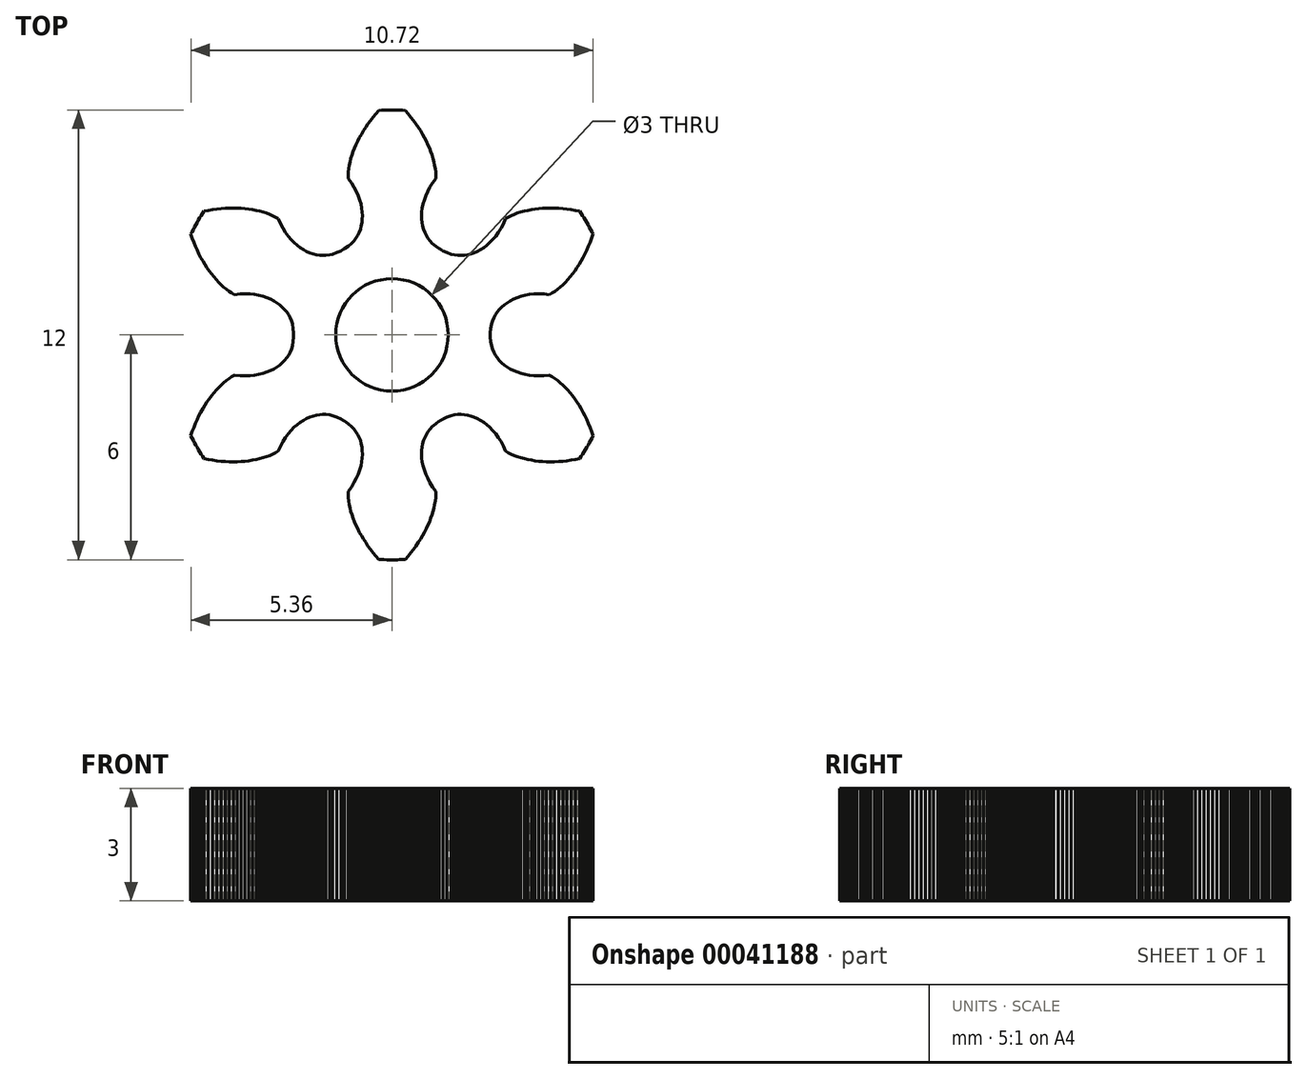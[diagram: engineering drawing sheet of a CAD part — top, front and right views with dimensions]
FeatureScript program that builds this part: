
annotation { "Feature Type Name" : "Feature", "Feature Type Description" : "" }
export const myFeature = defineFeature(function(context is Context, id is Id, definition is map)
    precondition{}
    {
        {
            var Q0;
            Q0=qCreatedBy(makeId("Top.planeOp"),FACE);
            var sketch = newSketch(context, id + "F0", { "sketchPlane" : qUnion([Q0])});
            skLineSegment(sketch, "E0", {"start": v(2.62, 0) * mm, "end": v(2.62, 0.01) * mm});
            skLineSegment(sketch, "E1", {"start": v(2.62, 0.01) * mm, "end": v(2.62, 0.02) * mm});
            skLineSegment(sketch, "E2", {"start": v(2.62, 0.02) * mm, "end": v(2.62, 0.03) * mm});
            skLineSegment(sketch, "E3", {"start": v(2.62, 0.03) * mm, "end": v(2.62, 0.05) * mm});
            skLineSegment(sketch, "E4", {"start": v(2.62, 0.05) * mm, "end": v(2.62, 0.06) * mm});
            skLineSegment(sketch, "E5", {"start": v(2.62, 0.06) * mm, "end": v(2.63, 0.17) * mm});
            skLineSegment(sketch, "E6", {"start": v(2.63, 0.17) * mm, "end": v(2.65, 0.3) * mm});
            skLineSegment(sketch, "E7", {"start": v(2.65, 0.3) * mm, "end": v(2.68, 0.38) * mm});
            skLineSegment(sketch, "E8", {"start": v(2.68, 0.38) * mm, "end": v(2.72, 0.46) * mm});
            skLineSegment(sketch, "E9", {"start": v(2.72, 0.46) * mm, "end": v(2.76, 0.54) * mm});
            skLineSegment(sketch, "E10", {"start": v(2.76, 0.54) * mm, "end": v(2.8, 0.6) * mm});
            skLineSegment(sketch, "E11", {"start": v(2.8, 0.6) * mm, "end": v(2.86, 0.68) * mm});
            skLineSegment(sketch, "E12", {"start": v(2.86, 0.68) * mm, "end": v(2.93, 0.74) * mm});
            skLineSegment(sketch, "E13", {"start": v(2.93, 0.74) * mm, "end": v(3, 0.8) * mm});
            skLineSegment(sketch, "E14", {"start": v(3, 0.8) * mm, "end": v(3.07, 0.86) * mm});
            skLineSegment(sketch, "E15", {"start": v(3.07, 0.86) * mm, "end": v(3.15, 0.9) * mm});
            skLineSegment(sketch, "E16", {"start": v(3.15, 0.9) * mm, "end": v(3.24, 0.95) * mm});
            skLineSegment(sketch, "E17", {"start": v(3.24, 0.95) * mm, "end": v(3.34, 1) * mm});
            skLineSegment(sketch, "E18", {"start": v(3.34, 1) * mm, "end": v(3.44, 1.03) * mm});
            skLineSegment(sketch, "E19", {"start": v(3.44, 1.03) * mm, "end": v(3.55, 1.05) * mm});
            skLineSegment(sketch, "E20", {"start": v(3.55, 1.05) * mm, "end": v(3.66, 1.08) * mm});
            skLineSegment(sketch, "E21", {"start": v(3.66, 1.08) * mm, "end": v(3.79, 1.09) * mm});
            skLineSegment(sketch, "E22", {"start": v(3.79, 1.09) * mm, "end": v(3.92, 1.1) * mm});
            skLineSegment(sketch, "E23", {"start": v(3.92, 1.1) * mm, "end": v(4.05, 1.1) * mm});
            skLineSegment(sketch, "E24", {"start": v(4.05, 1.1) * mm, "end": v(4.2, 1.07) * mm});
            skLineSegment(sketch, "E25", {"start": v(4.2, 1.07) * mm, "end": v(4.27, 1.12) * mm});
            skLineSegment(sketch, "E26", {"start": v(4.27, 1.12) * mm, "end": v(4.35, 1.16) * mm});
            skLineSegment(sketch, "E27", {"start": v(4.35, 1.16) * mm, "end": v(4.42, 1.22) * mm});
            skLineSegment(sketch, "E28", {"start": v(4.42, 1.22) * mm, "end": v(4.49, 1.28) * mm});
            skLineSegment(sketch, "E29", {"start": v(4.49, 1.28) * mm, "end": v(4.56, 1.34) * mm});
            skLineSegment(sketch, "E30", {"start": v(4.56, 1.34) * mm, "end": v(4.62, 1.4) * mm});
            skLineSegment(sketch, "E31", {"start": v(4.62, 1.4) * mm, "end": v(4.69, 1.47) * mm});
            skLineSegment(sketch, "E32", {"start": v(4.69, 1.47) * mm, "end": v(4.75, 1.55) * mm});
            skLineSegment(sketch, "E33", {"start": v(4.75, 1.55) * mm, "end": v(4.82, 1.63) * mm});
            skLineSegment(sketch, "E34", {"start": v(4.82, 1.63) * mm, "end": v(4.88, 1.7) * mm});
            skLineSegment(sketch, "E35", {"start": v(4.88, 1.7) * mm, "end": v(4.93, 1.8) * mm});
            skLineSegment(sketch, "E36", {"start": v(4.93, 1.8) * mm, "end": v(5, 1.88) * mm});
            skLineSegment(sketch, "E37", {"start": v(5, 1.88) * mm, "end": v(5.05, 1.97) * mm});
            skLineSegment(sketch, "E38", {"start": v(5.05, 1.97) * mm, "end": v(5.1, 2.06) * mm});
            skLineSegment(sketch, "E39", {"start": v(5.1, 2.06) * mm, "end": v(5.15, 2.16) * mm});
            skLineSegment(sketch, "E40", {"start": v(5.15, 2.16) * mm, "end": v(5.2, 2.26) * mm});
            skLineSegment(sketch, "E41", {"start": v(5.2, 2.26) * mm, "end": v(5.24, 2.36) * mm});
            skLineSegment(sketch, "E42", {"start": v(5.24, 2.36) * mm, "end": v(5.28, 2.47) * mm});
            skLineSegment(sketch, "E43", {"start": v(5.28, 2.47) * mm, "end": v(5.33, 2.58) * mm});
            skLineSegment(sketch, "E44", {"start": v(5.33, 2.58) * mm, "end": v(5.36, 2.69) * mm});
            skLineSegment(sketch, "E45", {"start": v(5.36, 2.69) * mm, "end": v(5.33, 2.75) * mm});
            skLineSegment(sketch, "E46", {"start": v(5.33, 2.75) * mm, "end": v(5.3, 2.81) * mm});
            skLineSegment(sketch, "E47", {"start": v(5.3, 2.81) * mm, "end": v(5.27, 2.88) * mm});
            skLineSegment(sketch, "E48", {"start": v(5.27, 2.88) * mm, "end": v(5.23, 2.94) * mm});
            skLineSegment(sketch, "E49", {"start": v(5.23, 2.94) * mm, "end": v(5.2, 3) * mm});
            skPoint(sketch, "E50", {"position": v(0, 0) * mm});
            skLineSegment(sketch, "E51", {"start": v(0, 0) * mm, "end": v(4.5, 0) * mm, "construction": true});
            skLineSegment(sketch, "E52", {"start": v(4.5, 0) * mm, "end": v(5.4, 0) * mm, "construction": true});
            skLineSegment(sketch, "E53.MirrorCS", {"start": v(2.62, 0) * mm, "end": v(2.62, -0.01) * mm});
            skLineSegment(sketch, "E54.MirrorCS", {"start": v(2.62, -0.01) * mm, "end": v(2.62, -0.02) * mm});
            skLineSegment(sketch, "E55.MirrorCS", {"start": v(2.62, -0.02) * mm, "end": v(2.62, -0.03) * mm});
            skLineSegment(sketch, "E56.MirrorCS", {"start": v(2.62, -0.05) * mm, "end": v(2.62, -0.06) * mm});
            skLineSegment(sketch, "E57.MirrorCS", {"start": v(2.62, -0.03) * mm, "end": v(2.62, -0.05) * mm});
            skLineSegment(sketch, "E58.MirrorCS", {"start": v(2.62, -0.06) * mm, "end": v(2.63, -0.17) * mm});
            skLineSegment(sketch, "E59.MirrorCS", {"start": v(3.55, -1.05) * mm, "end": v(3.66, -1.08) * mm});
            skLineSegment(sketch, "E60.MirrorCS", {"start": v(3.92, -1.1) * mm, "end": v(4.05, -1.1) * mm});
            skLineSegment(sketch, "E61.MirrorCS", {"start": v(3.66, -1.08) * mm, "end": v(3.79, -1.09) * mm});
            skLineSegment(sketch, "E62.MirrorCS", {"start": v(3.79, -1.09) * mm, "end": v(3.92, -1.1) * mm});
            skLineSegment(sketch, "E63.MirrorCS", {"start": v(5.33, -2.75) * mm, "end": v(5.3, -2.81) * mm});
            skLineSegment(sketch, "E64.MirrorCS", {"start": v(4.49, -1.28) * mm, "end": v(4.56, -1.34) * mm});
            skLineSegment(sketch, "E65.MirrorCS", {"start": v(4.27, -1.12) * mm, "end": v(4.35, -1.16) * mm});
            skLineSegment(sketch, "E66.MirrorCS", {"start": v(4.82, -1.63) * mm, "end": v(4.88, -1.7) * mm});
            skLineSegment(sketch, "E67.MirrorCS", {"start": v(4.35, -1.16) * mm, "end": v(4.42, -1.22) * mm});
            skLineSegment(sketch, "E68.MirrorCS", {"start": v(4.93, -1.8) * mm, "end": v(5, -1.88) * mm});
            skLineSegment(sketch, "E69.MirrorCS", {"start": v(5.1, -2.06) * mm, "end": v(5.15, -2.16) * mm});
            skLineSegment(sketch, "E70.MirrorCS", {"start": v(2.86, -0.68) * mm, "end": v(2.93, -0.74) * mm});
            skLineSegment(sketch, "E71.MirrorCS", {"start": v(3.44, -1.03) * mm, "end": v(3.55, -1.05) * mm});
            skLineSegment(sketch, "E72.MirrorCS", {"start": v(2.8, -0.6) * mm, "end": v(2.86, -0.68) * mm});
            skLineSegment(sketch, "E73.MirrorCS", {"start": v(5, -1.88) * mm, "end": v(5.05, -1.97) * mm});
            skLineSegment(sketch, "E74.MirrorCS", {"start": v(2.72, -0.46) * mm, "end": v(2.76, -0.54) * mm});
            skLineSegment(sketch, "E75.MirrorCS", {"start": v(3.24, -0.95) * mm, "end": v(3.34, -1) * mm});
            skLineSegment(sketch, "E76.MirrorCS", {"start": v(2.68, -0.38) * mm, "end": v(2.72, -0.46) * mm});
            skLineSegment(sketch, "E77.MirrorCS", {"start": v(2.65, -0.3) * mm, "end": v(2.68, -0.38) * mm});
            skLineSegment(sketch, "E78.MirrorCS", {"start": v(2.63, -0.17) * mm, "end": v(2.65, -0.3) * mm});
            skLineSegment(sketch, "E79.MirrorCS", {"start": v(2.76, -0.54) * mm, "end": v(2.8, -0.6) * mm});
            skLineSegment(sketch, "E80.MirrorCS", {"start": v(5.24, -2.36) * mm, "end": v(5.28, -2.47) * mm});
            skLineSegment(sketch, "E81.MirrorCS", {"start": v(2.93, -0.74) * mm, "end": v(3, -0.8) * mm});
            skLineSegment(sketch, "E82.MirrorCS", {"start": v(4.88, -1.7) * mm, "end": v(4.93, -1.8) * mm});
            skLineSegment(sketch, "E83.MirrorCS", {"start": v(4.69, -1.47) * mm, "end": v(4.75, -1.55) * mm});
            skLineSegment(sketch, "E84.MirrorCS", {"start": v(5.27, -2.88) * mm, "end": v(5.23, -2.94) * mm});
            skLineSegment(sketch, "E85.MirrorCS", {"start": v(4.75, -1.55) * mm, "end": v(4.82, -1.63) * mm});
            skLineSegment(sketch, "E86.MirrorCS", {"start": v(3, -0.8) * mm, "end": v(3.07, -0.86) * mm});
            skLineSegment(sketch, "E87.MirrorCS", {"start": v(5.23, -2.94) * mm, "end": v(5.2, -3) * mm});
            skLineSegment(sketch, "E88.MirrorCS", {"start": v(3.07, -0.86) * mm, "end": v(3.15, -0.9) * mm});
            skLineSegment(sketch, "E89.MirrorCS", {"start": v(5.05, -1.97) * mm, "end": v(5.1, -2.06) * mm});
            skLineSegment(sketch, "E90.MirrorCS", {"start": v(5.15, -2.16) * mm, "end": v(5.2, -2.26) * mm});
            skLineSegment(sketch, "E91.MirrorCS", {"start": v(4.42, -1.22) * mm, "end": v(4.49, -1.28) * mm});
            skLineSegment(sketch, "E92.MirrorCS", {"start": v(4.05, -1.1) * mm, "end": v(4.2, -1.07) * mm});
            skLineSegment(sketch, "E93.MirrorCS", {"start": v(5.33, -2.58) * mm, "end": v(5.36, -2.69) * mm});
            skLineSegment(sketch, "E94.MirrorCS", {"start": v(4.56, -1.34) * mm, "end": v(4.62, -1.4) * mm});
            skLineSegment(sketch, "E95.MirrorCS", {"start": v(4.2, -1.07) * mm, "end": v(4.27, -1.12) * mm});
            skLineSegment(sketch, "E96.MirrorCS", {"start": v(5.2, -2.26) * mm, "end": v(5.24, -2.36) * mm});
            skLineSegment(sketch, "E97.MirrorCS", {"start": v(3.34, -1) * mm, "end": v(3.44, -1.03) * mm});
            skLineSegment(sketch, "E98.MirrorCS", {"start": v(4.62, -1.4) * mm, "end": v(4.69, -1.47) * mm});
            skLineSegment(sketch, "E99.MirrorCS", {"start": v(5.28, -2.47) * mm, "end": v(5.33, -2.58) * mm});
            skLineSegment(sketch, "E100.MirrorCS", {"start": v(5.3, -2.81) * mm, "end": v(5.27, -2.88) * mm});
            skLineSegment(sketch, "E101.MirrorCS", {"start": v(3.15, -0.9) * mm, "end": v(3.24, -0.95) * mm});
            skLineSegment(sketch, "E102.MirrorCS", {"start": v(5.36, -2.69) * mm, "end": v(5.33, -2.75) * mm});
            skLineSegment(sketch, "E103.1.0", {"start": v(3.03, 3.1) * mm, "end": v(3.1, 3.14) * mm});
            skLineSegment(sketch, "E103.1.1", {"start": v(1.12, 4.61) * mm, "end": v(1.1, 4.7) * mm});
            skLineSegment(sketch, "E103.1.2", {"start": v(4.9, 3.32) * mm, "end": v(5.01, 3.3) * mm});
            skLineSegment(sketch, "E103.1.3", {"start": v(1.85, 2.12) * mm, "end": v(1.93, 2.13) * mm});
            skLineSegment(sketch, "E103.1.4", {"start": v(5.05, 3.24) * mm, "end": v(5.09, 3.18) * mm});
            skLineSegment(sketch, "E103.1.5", {"start": v(1.15, 4.43) * mm, "end": v(1.14, 4.52) * mm});
            skLineSegment(sketch, "E103.1.6", {"start": v(0.28, 6) * mm, "end": v(0.21, 6) * mm});
            skLineSegment(sketch, "E103.1.7", {"start": v(0.7, 5.54) * mm, "end": v(0.64, 5.63) * mm});
            skLineSegment(sketch, "E103.1.8", {"start": v(1.08, 4.06) * mm, "end": v(1.17, 4.17) * mm});
            skLineSegment(sketch, "E103.1.9", {"start": v(4.23, 3.38) * mm, "end": v(4.34, 3.38) * mm});
            skLineSegment(sketch, "E103.1.10", {"start": v(1.58, 2.15) * mm, "end": v(1.67, 2.13) * mm});
            skLineSegment(sketch, "E103.1.11", {"start": v(0.43, 5.9) * mm, "end": v(0.35, 5.99) * mm});
            skLineSegment(sketch, "E103.1.12", {"start": v(0.64, 5.63) * mm, "end": v(0.57, 5.72) * mm});
            skLineSegment(sketch, "E103.1.13", {"start": v(4.67, 3.36) * mm, "end": v(4.78, 3.34) * mm});
            skLineSegment(sketch, "E103.1.14", {"start": v(0.57, 5.72) * mm, "end": v(0.5, 5.81) * mm});
            skLineSegment(sketch, "E103.1.15", {"start": v(1.17, 4.26) * mm, "end": v(1.16, 4.35) * mm});
            skLineSegment(sketch, "E103.1.16", {"start": v(3.26, 3.22) * mm, "end": v(3.35, 3.25) * mm});
            skLineSegment(sketch, "E103.1.17", {"start": v(2.45, 2.33) * mm, "end": v(2.53, 2.4) * mm});
            skLineSegment(sketch, "E103.1.18", {"start": v(2.9, 2.85) * mm, "end": v(2.97, 2.96) * mm});
            skLineSegment(sketch, "E103.1.19", {"start": v(0.5, 5.81) * mm, "end": v(0.43, 5.9) * mm});
            skLineSegment(sketch, "E103.1.20", {"start": v(1.16, 4.35) * mm, "end": v(1.15, 4.43) * mm});
            skLineSegment(sketch, "E103.1.21", {"start": v(1.67, 2.13) * mm, "end": v(1.76, 2.12) * mm});
            skLineSegment(sketch, "E103.1.22", {"start": v(2.97, 2.96) * mm, "end": v(3.03, 3.1) * mm});
            skLineSegment(sketch, "E103.1.23", {"start": v(2.84, 2.74) * mm, "end": v(2.9, 2.85) * mm});
            skLineSegment(sketch, "E103.1.24", {"start": v(0.35, 5.99) * mm, "end": v(0.28, 6) * mm});
            skLineSegment(sketch, "E103.1.25", {"start": v(1.14, 4.52) * mm, "end": v(1.12, 4.61) * mm});
            skLineSegment(sketch, "E103.1.26", {"start": v(3.44, 3.28) * mm, "end": v(3.53, 3.3) * mm});
            skLineSegment(sketch, "E103.1.27", {"start": v(3.35, 3.25) * mm, "end": v(3.44, 3.28) * mm});
            skLineSegment(sketch, "E103.1.28", {"start": v(0.21, 6) * mm, "end": v(0.14, 6) * mm});
            skLineSegment(sketch, "E103.1.29", {"start": v(4.56, 3.37) * mm, "end": v(4.67, 3.36) * mm});
            skLineSegment(sketch, "E103.1.30", {"start": v(1.1, 4.7) * mm, "end": v(1.07, 4.8) * mm});
            skLineSegment(sketch, "E103.1.31", {"start": v(0.82, 2.9) * mm, "end": v(0.8, 3) * mm});
            skLineSegment(sketch, "E103.1.32", {"start": v(0.8, 3) * mm, "end": v(0.8, 3.09) * mm});
            skLineSegment(sketch, "E103.1.33", {"start": v(0.8, 3.09) * mm, "end": v(0.8, 3.18) * mm});
            skLineSegment(sketch, "E103.1.34", {"start": v(0.95, 3.82) * mm, "end": v(1.01, 3.94) * mm});
            skLineSegment(sketch, "E103.1.35", {"start": v(2.61, 2.46) * mm, "end": v(2.69, 2.55) * mm});
            skLineSegment(sketch, "E103.1.36", {"start": v(0.82, 5.35) * mm, "end": v(0.76, 5.45) * mm});
            skLineSegment(sketch, "E103.1.37", {"start": v(1.17, 2.37) * mm, "end": v(1.07, 2.44) * mm});
            skLineSegment(sketch, "E103.1.38", {"start": v(1.07, 2.44) * mm, "end": v(1.01, 2.5) * mm});
            skLineSegment(sketch, "E103.1.39", {"start": v(1.01, 2.5) * mm, "end": v(0.96, 2.58) * mm});
            skLineSegment(sketch, "E103.1.40", {"start": v(5.16, 3.06) * mm, "end": v(5.2, 3) * mm});
            skLineSegment(sketch, "E103.1.41", {"start": v(0.96, 2.58) * mm, "end": v(0.91, 2.66) * mm});
            skLineSegment(sketch, "E103.1.42", {"start": v(0.91, 2.66) * mm, "end": v(0.88, 2.74) * mm});
            skLineSegment(sketch, "E103.1.43", {"start": v(0.88, 2.74) * mm, "end": v(0.84, 2.82) * mm});
            skLineSegment(sketch, "E103.1.44", {"start": v(0.84, 2.82) * mm, "end": v(0.82, 2.9) * mm});
            skLineSegment(sketch, "E103.1.45", {"start": v(2.53, 2.4) * mm, "end": v(2.61, 2.46) * mm});
            skLineSegment(sketch, "E103.1.46", {"start": v(0.8, 3.18) * mm, "end": v(0.8, 3.28) * mm});
            skLineSegment(sketch, "E103.1.47", {"start": v(2.1, 2.16) * mm, "end": v(2.2, 2.2) * mm});
            skLineSegment(sketch, "E103.1.48", {"start": v(0.14, 6) * mm, "end": v(0.07, 6) * mm});
            skLineSegment(sketch, "E103.1.49", {"start": v(3.1, 3.14) * mm, "end": v(3.18, 3.18) * mm});
            skLineSegment(sketch, "E103.1.50", {"start": v(1.07, 4.8) * mm, "end": v(1.04, 4.9) * mm});
            skLineSegment(sketch, "E103.1.51", {"start": v(1.01, 3.94) * mm, "end": v(1.08, 4.06) * mm});
            skLineSegment(sketch, "E103.1.52", {"start": v(0.76, 5.45) * mm, "end": v(0.7, 5.54) * mm});
            skLineSegment(sketch, "E103.1.53", {"start": v(2.28, 2.23) * mm, "end": v(2.36, 2.28) * mm});
            skLineSegment(sketch, "E103.1.54", {"start": v(1.93, 2.13) * mm, "end": v(2.02, 2.14) * mm});
            skLineSegment(sketch, "E103.1.55", {"start": v(0.8, 3.28) * mm, "end": v(0.8, 3.39) * mm});
            skLineSegment(sketch, "E103.1.56", {"start": v(3.92, 3.37) * mm, "end": v(4.02, 3.38) * mm});
            skLineSegment(sketch, "E103.1.57", {"start": v(3.82, 3.36) * mm, "end": v(3.92, 3.37) * mm});
            skLineSegment(sketch, "E103.1.58", {"start": v(0.07, 6) * mm, "end": v(0, 6) * mm});
            skLineSegment(sketch, "E103.1.59", {"start": v(1.04, 4.9) * mm, "end": v(1, 4.98) * mm});
            skLineSegment(sketch, "E103.1.60", {"start": v(3.53, 3.3) * mm, "end": v(3.62, 3.32) * mm});
            skLineSegment(sketch, "E103.1.61", {"start": v(3.18, 3.18) * mm, "end": v(3.26, 3.22) * mm});
            skLineSegment(sketch, "E103.1.62", {"start": v(4.12, 3.38) * mm, "end": v(4.23, 3.38) * mm});
            skLineSegment(sketch, "E103.1.63", {"start": v(3.62, 3.32) * mm, "end": v(3.72, 3.34) * mm});
            skLineSegment(sketch, "E103.1.64", {"start": v(0.8, 3.39) * mm, "end": v(0.83, 3.5) * mm});
            skLineSegment(sketch, "E103.1.65", {"start": v(1, 4.98) * mm, "end": v(0.96, 5.08) * mm});
            skLineSegment(sketch, "E103.1.66", {"start": v(4.78, 3.34) * mm, "end": v(4.9, 3.32) * mm});
            skLineSegment(sketch, "E103.1.67", {"start": v(0.83, 3.5) * mm, "end": v(0.86, 3.6) * mm});
            skLineSegment(sketch, "E103.1.68", {"start": v(5.12, 3.12) * mm, "end": v(5.16, 3.06) * mm});
            skLineSegment(sketch, "E103.1.69", {"start": v(4.02, 3.38) * mm, "end": v(4.12, 3.38) * mm});
            skLineSegment(sketch, "E103.1.70", {"start": v(0.96, 5.08) * mm, "end": v(0.92, 5.17) * mm});
            skLineSegment(sketch, "E103.1.71", {"start": v(5.09, 3.18) * mm, "end": v(5.12, 3.12) * mm});
            skLineSegment(sketch, "E103.1.72", {"start": v(0.86, 3.6) * mm, "end": v(0.9, 3.71) * mm});
            skLineSegment(sketch, "E103.1.73", {"start": v(4.34, 3.38) * mm, "end": v(4.45, 3.38) * mm});
            skLineSegment(sketch, "E103.1.74", {"start": v(3.72, 3.34) * mm, "end": v(3.82, 3.36) * mm});
            skLineSegment(sketch, "E103.1.75", {"start": v(0.92, 5.17) * mm, "end": v(0.87, 5.26) * mm});
            skLineSegment(sketch, "E103.1.76", {"start": v(2.36, 2.28) * mm, "end": v(2.45, 2.33) * mm});
            skLineSegment(sketch, "E103.1.77", {"start": v(4.45, 3.38) * mm, "end": v(4.56, 3.37) * mm});
            skLineSegment(sketch, "E103.1.78", {"start": v(1.17, 4.17) * mm, "end": v(1.17, 4.26) * mm});
            skLineSegment(sketch, "E103.1.79", {"start": v(1.76, 2.12) * mm, "end": v(1.85, 2.12) * mm});
            skLineSegment(sketch, "E103.1.80", {"start": v(0.9, 3.71) * mm, "end": v(0.95, 3.82) * mm});
            skLineSegment(sketch, "E103.1.81", {"start": v(2.2, 2.2) * mm, "end": v(2.28, 2.23) * mm});
            skLineSegment(sketch, "E103.1.82", {"start": v(2.02, 2.14) * mm, "end": v(2.1, 2.16) * mm});
            skLineSegment(sketch, "E103.1.83", {"start": v(0.87, 5.26) * mm, "end": v(0.82, 5.35) * mm});
            skLineSegment(sketch, "E103.1.84", {"start": v(5.01, 3.3) * mm, "end": v(5.05, 3.24) * mm});
            skLineSegment(sketch, "E103.1.85", {"start": v(2.76, 2.64) * mm, "end": v(2.84, 2.74) * mm});
            skLineSegment(sketch, "E103.1.86", {"start": v(2.69, 2.55) * mm, "end": v(2.76, 2.64) * mm});
            skLineSegment(sketch, "E103.1.87", {"start": v(1.47, 2.2) * mm, "end": v(1.58, 2.15) * mm});
            skLineSegment(sketch, "E103.1.88", {"start": v(1.36, 2.24) * mm, "end": v(1.47, 2.2) * mm});
            skLineSegment(sketch, "E103.1.89", {"start": v(1.34, 2.26) * mm, "end": v(1.35, 2.25) * mm});
            skLineSegment(sketch, "E103.1.90", {"start": v(1.31, 2.27) * mm, "end": v(1.3, 2.28) * mm});
            skLineSegment(sketch, "E103.1.91", {"start": v(1.27, 2.3) * mm, "end": v(1.26, 2.3) * mm});
            skLineSegment(sketch, "E103.1.92", {"start": v(1.26, 2.3) * mm, "end": v(1.17, 2.37) * mm});
            skLineSegment(sketch, "E103.1.93", {"start": v(1.28, 2.3) * mm, "end": v(1.27, 2.3) * mm});
            skLineSegment(sketch, "E103.1.94", {"start": v(1.3, 2.28) * mm, "end": v(1.28, 2.3) * mm});
            skLineSegment(sketch, "E103.1.95", {"start": v(1.3, 2.28) * mm, "end": v(1.3, 2.28) * mm});
            skLineSegment(sketch, "E103.1.96", {"start": v(1.31, 2.27) * mm, "end": v(1.32, 2.27) * mm});
            skLineSegment(sketch, "E103.1.97", {"start": v(1.32, 2.27) * mm, "end": v(1.33, 2.26) * mm});
            skLineSegment(sketch, "E103.1.98", {"start": v(1.33, 2.26) * mm, "end": v(1.34, 2.26) * mm});
            skLineSegment(sketch, "E103.1.99", {"start": v(1.35, 2.25) * mm, "end": v(1.36, 2.24) * mm});
            skLineSegment(sketch, "E103.2.0", {"start": v(-1.17, 4.17) * mm, "end": v(-1.17, 4.26) * mm});
            skLineSegment(sketch, "E103.2.1", {"start": v(-3.44, 3.28) * mm, "end": v(-3.53, 3.3) * mm});
            skLineSegment(sketch, "E103.2.2", {"start": v(-0.43, 5.9) * mm, "end": v(-0.35, 5.99) * mm});
            skLineSegment(sketch, "E103.2.3", {"start": v(-0.91, 2.66) * mm, "end": v(-0.88, 2.74) * mm});
            skLineSegment(sketch, "E103.2.4", {"start": v(-0.28, 6) * mm, "end": v(-0.21, 6) * mm});
            skLineSegment(sketch, "E103.2.5", {"start": v(-3.26, 3.22) * mm, "end": v(-3.35, 3.25) * mm});
            skLineSegment(sketch, "E103.2.6", {"start": v(-5.05, 3.24) * mm, "end": v(-5.09, 3.18) * mm});
            skLineSegment(sketch, "E103.2.7", {"start": v(-4.45, 3.38) * mm, "end": v(-4.56, 3.37) * mm});
            skLineSegment(sketch, "E103.2.8", {"start": v(-2.97, 2.96) * mm, "end": v(-3.03, 3.1) * mm});
            skLineSegment(sketch, "E103.2.9", {"start": v(-0.82, 5.35) * mm, "end": v(-0.76, 5.45) * mm});
            skLineSegment(sketch, "E103.2.10", {"start": v(-1.07, 2.44) * mm, "end": v(-1.01, 2.5) * mm});
            skLineSegment(sketch, "E103.2.11", {"start": v(-4.9, 3.32) * mm, "end": v(-5.01, 3.3) * mm});
            skLineSegment(sketch, "E103.2.12", {"start": v(-4.56, 3.37) * mm, "end": v(-4.67, 3.36) * mm});
            skLineSegment(sketch, "E103.2.13", {"start": v(-0.57, 5.72) * mm, "end": v(-0.5, 5.81) * mm});
            skLineSegment(sketch, "E103.2.14", {"start": v(-4.67, 3.36) * mm, "end": v(-4.78, 3.34) * mm});
            skLineSegment(sketch, "E103.2.15", {"start": v(-3.1, 3.14) * mm, "end": v(-3.18, 3.18) * mm});
            skLineSegment(sketch, "E103.2.16", {"start": v(-1.15, 4.43) * mm, "end": v(-1.14, 4.52) * mm});
            skLineSegment(sketch, "E103.2.17", {"start": v(-0.8, 3.28) * mm, "end": v(-0.8, 3.39) * mm});
            skLineSegment(sketch, "E103.2.18", {"start": v(-1.01, 3.94) * mm, "end": v(-1.08, 4.06) * mm});
            skLineSegment(sketch, "E103.2.19", {"start": v(-4.78, 3.34) * mm, "end": v(-4.9, 3.32) * mm});
            skLineSegment(sketch, "E103.2.20", {"start": v(-3.18, 3.18) * mm, "end": v(-3.26, 3.22) * mm});
            skLineSegment(sketch, "E103.2.21", {"start": v(-1.01, 2.5) * mm, "end": v(-0.96, 2.58) * mm});
            skLineSegment(sketch, "E103.2.22", {"start": v(-1.08, 4.06) * mm, "end": v(-1.17, 4.17) * mm});
            skLineSegment(sketch, "E103.2.23", {"start": v(-0.95, 3.82) * mm, "end": v(-1.01, 3.94) * mm});
            skLineSegment(sketch, "E103.2.24", {"start": v(-5.01, 3.3) * mm, "end": v(-5.05, 3.24) * mm});
            skLineSegment(sketch, "E103.2.25", {"start": v(-3.35, 3.25) * mm, "end": v(-3.44, 3.28) * mm});
            skLineSegment(sketch, "E103.2.26", {"start": v(-1.12, 4.61) * mm, "end": v(-1.1, 4.7) * mm});
            skLineSegment(sketch, "E103.2.27", {"start": v(-1.14, 4.52) * mm, "end": v(-1.12, 4.61) * mm});
            skLineSegment(sketch, "E103.2.28", {"start": v(-5.09, 3.18) * mm, "end": v(-5.12, 3.12) * mm});
            skLineSegment(sketch, "E103.2.29", {"start": v(-0.64, 5.63) * mm, "end": v(-0.57, 5.72) * mm});
            skLineSegment(sketch, "E103.2.30", {"start": v(-3.53, 3.3) * mm, "end": v(-3.62, 3.32) * mm});
            skLineSegment(sketch, "E103.2.31", {"start": v(-2.1, 2.16) * mm, "end": v(-2.2, 2.2) * mm});
            skLineSegment(sketch, "E103.2.32", {"start": v(-2.2, 2.2) * mm, "end": v(-2.28, 2.23) * mm});
            skLineSegment(sketch, "E103.2.33", {"start": v(-2.28, 2.23) * mm, "end": v(-2.36, 2.28) * mm});
            skLineSegment(sketch, "E103.2.34", {"start": v(-2.84, 2.74) * mm, "end": v(-2.9, 2.85) * mm});
            skLineSegment(sketch, "E103.2.35", {"start": v(-0.83, 3.5) * mm, "end": v(-0.86, 3.6) * mm});
            skLineSegment(sketch, "E103.2.36", {"start": v(-4.23, 3.38) * mm, "end": v(-4.34, 3.38) * mm});
            skLineSegment(sketch, "E103.2.37", {"start": v(-1.47, 2.2) * mm, "end": v(-1.58, 2.15) * mm});
            skLineSegment(sketch, "E103.2.38", {"start": v(-1.58, 2.15) * mm, "end": v(-1.67, 2.13) * mm});
            skLineSegment(sketch, "E103.2.39", {"start": v(-1.67, 2.13) * mm, "end": v(-1.76, 2.12) * mm});
            skLineSegment(sketch, "E103.2.40", {"start": v(-0.07, 6) * mm, "end": v(0, 6) * mm});
            skLineSegment(sketch, "E103.2.41", {"start": v(-1.76, 2.12) * mm, "end": v(-1.85, 2.12) * mm});
            skLineSegment(sketch, "E103.2.42", {"start": v(-1.85, 2.12) * mm, "end": v(-1.93, 2.13) * mm});
            skLineSegment(sketch, "E103.2.43", {"start": v(-1.93, 2.13) * mm, "end": v(-2.02, 2.14) * mm});
            skLineSegment(sketch, "E103.2.44", {"start": v(-2.02, 2.14) * mm, "end": v(-2.1, 2.16) * mm});
            skLineSegment(sketch, "E103.2.45", {"start": v(-0.8, 3.39) * mm, "end": v(-0.83, 3.5) * mm});
            skLineSegment(sketch, "E103.2.46", {"start": v(-2.36, 2.28) * mm, "end": v(-2.45, 2.33) * mm});
            skLineSegment(sketch, "E103.2.47", {"start": v(-0.82, 2.9) * mm, "end": v(-0.8, 3) * mm});
            skLineSegment(sketch, "E103.2.48", {"start": v(-5.12, 3.12) * mm, "end": v(-5.16, 3.06) * mm});
            skLineSegment(sketch, "E103.2.49", {"start": v(-1.17, 4.26) * mm, "end": v(-1.16, 4.35) * mm});
            skLineSegment(sketch, "E103.2.50", {"start": v(-3.62, 3.32) * mm, "end": v(-3.72, 3.34) * mm});
            skLineSegment(sketch, "E103.2.51", {"start": v(-2.9, 2.85) * mm, "end": v(-2.97, 2.96) * mm});
            skLineSegment(sketch, "E103.2.52", {"start": v(-4.34, 3.38) * mm, "end": v(-4.45, 3.38) * mm});
            skLineSegment(sketch, "E103.2.53", {"start": v(-0.8, 3.09) * mm, "end": v(-0.8, 3.18) * mm});
            skLineSegment(sketch, "E103.2.54", {"start": v(-0.88, 2.74) * mm, "end": v(-0.84, 2.82) * mm});
            skLineSegment(sketch, "E103.2.55", {"start": v(-2.45, 2.33) * mm, "end": v(-2.53, 2.4) * mm});
            skLineSegment(sketch, "E103.2.56", {"start": v(-0.96, 5.08) * mm, "end": v(-0.92, 5.17) * mm});
            skLineSegment(sketch, "E103.2.57", {"start": v(-1, 4.98) * mm, "end": v(-0.96, 5.08) * mm});
            skLineSegment(sketch, "E103.2.58", {"start": v(-5.16, 3.06) * mm, "end": v(-5.2, 3) * mm});
            skLineSegment(sketch, "E103.2.59", {"start": v(-3.72, 3.34) * mm, "end": v(-3.82, 3.36) * mm});
            skLineSegment(sketch, "E103.2.60", {"start": v(-1.1, 4.7) * mm, "end": v(-1.07, 4.8) * mm});
            skLineSegment(sketch, "E103.2.61", {"start": v(-1.16, 4.35) * mm, "end": v(-1.15, 4.43) * mm});
            skLineSegment(sketch, "E103.2.62", {"start": v(-0.87, 5.26) * mm, "end": v(-0.82, 5.35) * mm});
            skLineSegment(sketch, "E103.2.63", {"start": v(-1.07, 4.8) * mm, "end": v(-1.04, 4.9) * mm});
            skLineSegment(sketch, "E103.2.64", {"start": v(-2.53, 2.4) * mm, "end": v(-2.61, 2.46) * mm});
            skLineSegment(sketch, "E103.2.65", {"start": v(-3.82, 3.36) * mm, "end": v(-3.92, 3.37) * mm});
            skLineSegment(sketch, "E103.2.66", {"start": v(-0.5, 5.81) * mm, "end": v(-0.43, 5.9) * mm});
            skLineSegment(sketch, "E103.2.67", {"start": v(-2.61, 2.46) * mm, "end": v(-2.69, 2.55) * mm});
            skLineSegment(sketch, "E103.2.68", {"start": v(-0.14, 6) * mm, "end": v(-0.07, 6) * mm});
            skLineSegment(sketch, "E103.2.69", {"start": v(-0.92, 5.17) * mm, "end": v(-0.87, 5.26) * mm});
            skLineSegment(sketch, "E103.2.70", {"start": v(-3.92, 3.37) * mm, "end": v(-4.02, 3.38) * mm});
            skLineSegment(sketch, "E103.2.71", {"start": v(-0.21, 6) * mm, "end": v(-0.14, 6) * mm});
            skLineSegment(sketch, "E103.2.72", {"start": v(-2.69, 2.55) * mm, "end": v(-2.76, 2.64) * mm});
            skLineSegment(sketch, "E103.2.73", {"start": v(-0.76, 5.45) * mm, "end": v(-0.7, 5.54) * mm});
            skLineSegment(sketch, "E103.2.74", {"start": v(-1.04, 4.9) * mm, "end": v(-1, 4.98) * mm});
            skLineSegment(sketch, "E103.2.75", {"start": v(-4.02, 3.38) * mm, "end": v(-4.12, 3.38) * mm});
            skLineSegment(sketch, "E103.2.76", {"start": v(-0.8, 3.18) * mm, "end": v(-0.8, 3.28) * mm});
            skLineSegment(sketch, "E103.2.77", {"start": v(-0.7, 5.54) * mm, "end": v(-0.64, 5.63) * mm});
            skLineSegment(sketch, "E103.2.78", {"start": v(-3.03, 3.1) * mm, "end": v(-3.1, 3.14) * mm});
            skLineSegment(sketch, "E103.2.79", {"start": v(-0.96, 2.58) * mm, "end": v(-0.91, 2.66) * mm});
            skLineSegment(sketch, "E103.2.80", {"start": v(-2.76, 2.64) * mm, "end": v(-2.84, 2.74) * mm});
            skLineSegment(sketch, "E103.2.81", {"start": v(-0.8, 3) * mm, "end": v(-0.8, 3.09) * mm});
            skLineSegment(sketch, "E103.2.82", {"start": v(-0.84, 2.82) * mm, "end": v(-0.82, 2.9) * mm});
            skLineSegment(sketch, "E103.2.83", {"start": v(-4.12, 3.38) * mm, "end": v(-4.23, 3.38) * mm});
            skLineSegment(sketch, "E103.2.84", {"start": v(-0.35, 5.99) * mm, "end": v(-0.28, 6) * mm});
            skLineSegment(sketch, "E103.2.85", {"start": v(-0.9, 3.71) * mm, "end": v(-0.95, 3.82) * mm});
            skLineSegment(sketch, "E103.2.86", {"start": v(-0.86, 3.6) * mm, "end": v(-0.9, 3.71) * mm});
            skLineSegment(sketch, "E103.2.87", {"start": v(-1.17, 2.37) * mm, "end": v(-1.07, 2.44) * mm});
            skLineSegment(sketch, "E103.2.88", {"start": v(-1.26, 2.3) * mm, "end": v(-1.17, 2.37) * mm});
            skLineSegment(sketch, "E103.2.89", {"start": v(-1.28, 2.3) * mm, "end": v(-1.27, 2.3) * mm});
            skLineSegment(sketch, "E103.2.90", {"start": v(-1.31, 2.27) * mm, "end": v(-1.32, 2.27) * mm});
            skLineSegment(sketch, "E103.2.91", {"start": v(-1.35, 2.25) * mm, "end": v(-1.36, 2.24) * mm});
            skLineSegment(sketch, "E103.2.92", {"start": v(-1.36, 2.24) * mm, "end": v(-1.47, 2.2) * mm});
            skLineSegment(sketch, "E103.2.93", {"start": v(-1.34, 2.26) * mm, "end": v(-1.35, 2.25) * mm});
            skLineSegment(sketch, "E103.2.94", {"start": v(-1.33, 2.26) * mm, "end": v(-1.34, 2.26) * mm});
            skLineSegment(sketch, "E103.2.95", {"start": v(-1.32, 2.27) * mm, "end": v(-1.33, 2.26) * mm});
            skLineSegment(sketch, "E103.2.96", {"start": v(-1.31, 2.27) * mm, "end": v(-1.3, 2.28) * mm});
            skLineSegment(sketch, "E103.2.97", {"start": v(-1.3, 2.28) * mm, "end": v(-1.3, 2.28) * mm});
            skLineSegment(sketch, "E103.2.98", {"start": v(-1.3, 2.28) * mm, "end": v(-1.28, 2.3) * mm});
            skLineSegment(sketch, "E103.2.99", {"start": v(-1.27, 2.3) * mm, "end": v(-1.26, 2.3) * mm});
            skLineSegment(sketch, "E103.3.0", {"start": v(-4.2, 1.07) * mm, "end": v(-4.27, 1.12) * mm});
            skLineSegment(sketch, "E103.3.1", {"start": v(-4.56, -1.34) * mm, "end": v(-4.62, -1.4) * mm});
            skLineSegment(sketch, "E103.3.2", {"start": v(-5.33, 2.58) * mm, "end": v(-5.36, 2.69) * mm});
            skLineSegment(sketch, "E103.3.3", {"start": v(-2.76, 0.54) * mm, "end": v(-2.8, 0.6) * mm});
            skLineSegment(sketch, "E103.3.4", {"start": v(-5.33, 2.75) * mm, "end": v(-5.3, 2.81) * mm});
            skLineSegment(sketch, "E103.3.5", {"start": v(-4.42, -1.22) * mm, "end": v(-4.49, -1.28) * mm});
            skLineSegment(sketch, "E103.3.6", {"start": v(-5.33, -2.75) * mm, "end": v(-5.3, -2.81) * mm});
            skLineSegment(sketch, "E103.3.7", {"start": v(-5.15, -2.16) * mm, "end": v(-5.2, -2.26) * mm});
            skLineSegment(sketch, "E103.3.8", {"start": v(-4.05, -1.1) * mm, "end": v(-4.2, -1.07) * mm});
            skLineSegment(sketch, "E103.3.9", {"start": v(-5.05, 1.97) * mm, "end": v(-5.1, 2.06) * mm});
            skLineSegment(sketch, "E103.3.10", {"start": v(-2.65, 0.3) * mm, "end": v(-2.68, 0.38) * mm});
            skLineSegment(sketch, "E103.3.11", {"start": v(-5.33, -2.58) * mm, "end": v(-5.36, -2.69) * mm});
            skLineSegment(sketch, "E103.3.12", {"start": v(-5.2, -2.26) * mm, "end": v(-5.24, -2.36) * mm});
            skLineSegment(sketch, "E103.3.13", {"start": v(-5.24, 2.36) * mm, "end": v(-5.28, 2.47) * mm});
            skLineSegment(sketch, "E103.3.14", {"start": v(-5.24, -2.36) * mm, "end": v(-5.28, -2.47) * mm});
            skLineSegment(sketch, "E103.3.15", {"start": v(-4.27, -1.12) * mm, "end": v(-4.35, -1.16) * mm});
            skLineSegment(sketch, "E103.3.16", {"start": v(-4.42, 1.22) * mm, "end": v(-4.49, 1.28) * mm});
            skLineSegment(sketch, "E103.3.17", {"start": v(-3.24, 0.95) * mm, "end": v(-3.34, 1) * mm});
            skLineSegment(sketch, "E103.3.18", {"start": v(-3.92, 1.1) * mm, "end": v(-4.05, 1.1) * mm});
            skLineSegment(sketch, "E103.3.19", {"start": v(-5.28, -2.47) * mm, "end": v(-5.33, -2.58) * mm});
            skLineSegment(sketch, "E103.3.20", {"start": v(-4.35, -1.16) * mm, "end": v(-4.42, -1.22) * mm});
            skLineSegment(sketch, "E103.3.21", {"start": v(-2.68, 0.38) * mm, "end": v(-2.72, 0.46) * mm});
            skLineSegment(sketch, "E103.3.22", {"start": v(-4.05, 1.1) * mm, "end": v(-4.2, 1.07) * mm});
            skLineSegment(sketch, "E103.3.23", {"start": v(-3.79, 1.09) * mm, "end": v(-3.92, 1.1) * mm});
            skLineSegment(sketch, "E103.3.24", {"start": v(-5.36, -2.69) * mm, "end": v(-5.33, -2.75) * mm});
            skLineSegment(sketch, "E103.3.25", {"start": v(-4.49, -1.28) * mm, "end": v(-4.56, -1.34) * mm});
            skLineSegment(sketch, "E103.3.26", {"start": v(-4.56, 1.34) * mm, "end": v(-4.62, 1.4) * mm});
            skLineSegment(sketch, "E103.3.27", {"start": v(-4.49, 1.28) * mm, "end": v(-4.56, 1.34) * mm});
            skLineSegment(sketch, "E103.3.28", {"start": v(-5.3, -2.81) * mm, "end": v(-5.27, -2.88) * mm});
            skLineSegment(sketch, "E103.3.29", {"start": v(-5.2, 2.26) * mm, "end": v(-5.24, 2.36) * mm});
            skLineSegment(sketch, "E103.3.30", {"start": v(-4.62, -1.4) * mm, "end": v(-4.69, -1.47) * mm});
            skLineSegment(sketch, "E103.3.31", {"start": v(-2.93, -0.74) * mm, "end": v(-3, -0.8) * mm});
            skLineSegment(sketch, "E103.3.32", {"start": v(-3, -0.8) * mm, "end": v(-3.07, -0.86) * mm});
            skLineSegment(sketch, "E103.3.33", {"start": v(-3.07, -0.86) * mm, "end": v(-3.15, -0.9) * mm});
            skLineSegment(sketch, "E103.3.34", {"start": v(-3.79, -1.09) * mm, "end": v(-3.92, -1.1) * mm});
            skLineSegment(sketch, "E103.3.35", {"start": v(-3.44, 1.03) * mm, "end": v(-3.55, 1.05) * mm});
            skLineSegment(sketch, "E103.3.36", {"start": v(-5.05, -1.97) * mm, "end": v(-5.1, -2.06) * mm});
            skLineSegment(sketch, "E103.3.37", {"start": v(-2.63, -0.17) * mm, "end": v(-2.65, -0.3) * mm});
            skLineSegment(sketch, "E103.3.38", {"start": v(-2.65, -0.3) * mm, "end": v(-2.68, -0.38) * mm});
            skLineSegment(sketch, "E103.3.39", {"start": v(-2.68, -0.38) * mm, "end": v(-2.72, -0.46) * mm});
            skLineSegment(sketch, "E103.3.40", {"start": v(-5.23, 2.94) * mm, "end": v(-5.2, 3) * mm});
            skLineSegment(sketch, "E103.3.41", {"start": v(-2.72, -0.46) * mm, "end": v(-2.76, -0.54) * mm});
            skLineSegment(sketch, "E103.3.42", {"start": v(-2.76, -0.54) * mm, "end": v(-2.8, -0.6) * mm});
            skLineSegment(sketch, "E103.3.43", {"start": v(-2.8, -0.6) * mm, "end": v(-2.86, -0.68) * mm});
            skLineSegment(sketch, "E103.3.44", {"start": v(-2.86, -0.68) * mm, "end": v(-2.93, -0.74) * mm});
            skLineSegment(sketch, "E103.3.45", {"start": v(-3.34, 1) * mm, "end": v(-3.44, 1.03) * mm});
            skLineSegment(sketch, "E103.3.46", {"start": v(-3.15, -0.9) * mm, "end": v(-3.24, -0.95) * mm});
            skLineSegment(sketch, "E103.3.47", {"start": v(-2.93, 0.74) * mm, "end": v(-3, 0.8) * mm});
            skLineSegment(sketch, "E103.3.48", {"start": v(-5.27, -2.88) * mm, "end": v(-5.23, -2.94) * mm});
            skLineSegment(sketch, "E103.3.49", {"start": v(-4.27, 1.12) * mm, "end": v(-4.35, 1.16) * mm});
            skLineSegment(sketch, "E103.3.50", {"start": v(-4.69, -1.47) * mm, "end": v(-4.75, -1.55) * mm});
            skLineSegment(sketch, "E103.3.51", {"start": v(-3.92, -1.1) * mm, "end": v(-4.05, -1.1) * mm});
            skLineSegment(sketch, "E103.3.52", {"start": v(-5.1, -2.06) * mm, "end": v(-5.15, -2.16) * mm});
            skLineSegment(sketch, "E103.3.53", {"start": v(-3.07, 0.86) * mm, "end": v(-3.15, 0.9) * mm});
            skLineSegment(sketch, "E103.3.54", {"start": v(-2.8, 0.6) * mm, "end": v(-2.86, 0.68) * mm});
            skLineSegment(sketch, "E103.3.55", {"start": v(-3.24, -0.95) * mm, "end": v(-3.34, -1) * mm});
            skLineSegment(sketch, "E103.3.56", {"start": v(-4.88, 1.7) * mm, "end": v(-4.93, 1.8) * mm});
            skLineSegment(sketch, "E103.3.57", {"start": v(-4.82, 1.63) * mm, "end": v(-4.88, 1.7) * mm});
            skLineSegment(sketch, "E103.3.58", {"start": v(-5.23, -2.94) * mm, "end": v(-5.2, -3) * mm});
            skLineSegment(sketch, "E103.3.59", {"start": v(-4.75, -1.55) * mm, "end": v(-4.82, -1.63) * mm});
            skLineSegment(sketch, "E103.3.60", {"start": v(-4.62, 1.4) * mm, "end": v(-4.69, 1.47) * mm});
            skLineSegment(sketch, "E103.3.61", {"start": v(-4.35, 1.16) * mm, "end": v(-4.42, 1.22) * mm});
            skLineSegment(sketch, "E103.3.62", {"start": v(-5, 1.88) * mm, "end": v(-5.05, 1.97) * mm});
            skLineSegment(sketch, "E103.3.63", {"start": v(-4.69, 1.47) * mm, "end": v(-4.75, 1.55) * mm});
            skLineSegment(sketch, "E103.3.64", {"start": v(-3.34, -1) * mm, "end": v(-3.44, -1.03) * mm});
            skLineSegment(sketch, "E103.3.65", {"start": v(-4.82, -1.63) * mm, "end": v(-4.88, -1.7) * mm});
            skLineSegment(sketch, "E103.3.66", {"start": v(-5.28, 2.47) * mm, "end": v(-5.33, 2.58) * mm});
            skLineSegment(sketch, "E103.3.67", {"start": v(-3.44, -1.03) * mm, "end": v(-3.55, -1.05) * mm});
            skLineSegment(sketch, "E103.3.68", {"start": v(-5.27, 2.88) * mm, "end": v(-5.23, 2.94) * mm});
            skLineSegment(sketch, "E103.3.69", {"start": v(-4.93, 1.8) * mm, "end": v(-5, 1.88) * mm});
            skLineSegment(sketch, "E103.3.70", {"start": v(-4.88, -1.7) * mm, "end": v(-4.93, -1.8) * mm});
            skLineSegment(sketch, "E103.3.71", {"start": v(-5.3, 2.81) * mm, "end": v(-5.27, 2.88) * mm});
            skLineSegment(sketch, "E103.3.72", {"start": v(-3.55, -1.05) * mm, "end": v(-3.66, -1.08) * mm});
            skLineSegment(sketch, "E103.3.73", {"start": v(-5.1, 2.06) * mm, "end": v(-5.15, 2.16) * mm});
            skLineSegment(sketch, "E103.3.74", {"start": v(-4.75, 1.55) * mm, "end": v(-4.82, 1.63) * mm});
            skLineSegment(sketch, "E103.3.75", {"start": v(-4.93, -1.8) * mm, "end": v(-5, -1.88) * mm});
            skLineSegment(sketch, "E103.3.76", {"start": v(-3.15, 0.9) * mm, "end": v(-3.24, 0.95) * mm});
            skLineSegment(sketch, "E103.3.77", {"start": v(-5.15, 2.16) * mm, "end": v(-5.2, 2.26) * mm});
            skLineSegment(sketch, "E103.3.78", {"start": v(-4.2, -1.07) * mm, "end": v(-4.27, -1.12) * mm});
            skLineSegment(sketch, "E103.3.79", {"start": v(-2.72, 0.46) * mm, "end": v(-2.76, 0.54) * mm});
            skLineSegment(sketch, "E103.3.80", {"start": v(-3.66, -1.08) * mm, "end": v(-3.79, -1.09) * mm});
            skLineSegment(sketch, "E103.3.81", {"start": v(-3, 0.8) * mm, "end": v(-3.07, 0.86) * mm});
            skLineSegment(sketch, "E103.3.82", {"start": v(-2.86, 0.68) * mm, "end": v(-2.93, 0.74) * mm});
            skLineSegment(sketch, "E103.3.83", {"start": v(-5, -1.88) * mm, "end": v(-5.05, -1.97) * mm});
            skLineSegment(sketch, "E103.3.84", {"start": v(-5.36, 2.69) * mm, "end": v(-5.33, 2.75) * mm});
            skLineSegment(sketch, "E103.3.85", {"start": v(-3.66, 1.08) * mm, "end": v(-3.79, 1.09) * mm});
            skLineSegment(sketch, "E103.3.86", {"start": v(-3.55, 1.05) * mm, "end": v(-3.66, 1.08) * mm});
            skLineSegment(sketch, "E103.3.87", {"start": v(-2.63, 0.17) * mm, "end": v(-2.65, 0.3) * mm});
            skLineSegment(sketch, "E103.3.88", {"start": v(-2.62, 0.06) * mm, "end": v(-2.63, 0.17) * mm});
            skLineSegment(sketch, "E103.3.89", {"start": v(-2.62, 0.03) * mm, "end": v(-2.62, 0.05) * mm});
            skLineSegment(sketch, "E103.3.90", {"start": v(-2.62, 0) * mm, "end": v(-2.62, -0.01) * mm});
            skLineSegment(sketch, "E103.3.91", {"start": v(-2.62, -0.05) * mm, "end": v(-2.62, -0.06) * mm});
            skLineSegment(sketch, "E103.3.92", {"start": v(-2.62, -0.06) * mm, "end": v(-2.63, -0.17) * mm});
            skLineSegment(sketch, "E103.3.93", {"start": v(-2.62, -0.03) * mm, "end": v(-2.62, -0.05) * mm});
            skLineSegment(sketch, "E103.3.94", {"start": v(-2.62, -0.02) * mm, "end": v(-2.62, -0.03) * mm});
            skLineSegment(sketch, "E103.3.95", {"start": v(-2.62, -0.01) * mm, "end": v(-2.62, -0.02) * mm});
            skLineSegment(sketch, "E103.3.96", {"start": v(-2.62, 0) * mm, "end": v(-2.62, 0.01) * mm});
            skLineSegment(sketch, "E103.3.97", {"start": v(-2.62, 0.01) * mm, "end": v(-2.62, 0.02) * mm});
            skLineSegment(sketch, "E103.3.98", {"start": v(-2.62, 0.02) * mm, "end": v(-2.62, 0.03) * mm});
            skLineSegment(sketch, "E103.3.99", {"start": v(-2.62, 0.05) * mm, "end": v(-2.62, 0.06) * mm});
            skLineSegment(sketch, "E103.4.0", {"start": v(-3.03, -3.1) * mm, "end": v(-3.1, -3.14) * mm});
            skLineSegment(sketch, "E103.4.1", {"start": v(-1.12, -4.61) * mm, "end": v(-1.1, -4.7) * mm});
            skLineSegment(sketch, "E103.4.2", {"start": v(-4.9, -3.32) * mm, "end": v(-5.01, -3.3) * mm});
            skLineSegment(sketch, "E103.4.3", {"start": v(-1.85, -2.12) * mm, "end": v(-1.93, -2.13) * mm});
            skLineSegment(sketch, "E103.4.4", {"start": v(-5.05, -3.24) * mm, "end": v(-5.09, -3.18) * mm});
            skLineSegment(sketch, "E103.4.5", {"start": v(-1.15, -4.43) * mm, "end": v(-1.14, -4.52) * mm});
            skLineSegment(sketch, "E103.4.6", {"start": v(-0.28, -6) * mm, "end": v(-0.21, -6) * mm});
            skLineSegment(sketch, "E103.4.7", {"start": v(-0.7, -5.54) * mm, "end": v(-0.64, -5.63) * mm});
            skLineSegment(sketch, "E103.4.8", {"start": v(-1.08, -4.06) * mm, "end": v(-1.17, -4.17) * mm});
            skLineSegment(sketch, "E103.4.9", {"start": v(-4.23, -3.38) * mm, "end": v(-4.34, -3.38) * mm});
            skLineSegment(sketch, "E103.4.10", {"start": v(-1.58, -2.15) * mm, "end": v(-1.67, -2.13) * mm});
            skLineSegment(sketch, "E103.4.11", {"start": v(-0.43, -5.9) * mm, "end": v(-0.35, -5.99) * mm});
            skLineSegment(sketch, "E103.4.12", {"start": v(-0.64, -5.63) * mm, "end": v(-0.57, -5.72) * mm});
            skLineSegment(sketch, "E103.4.13", {"start": v(-4.67, -3.36) * mm, "end": v(-4.78, -3.34) * mm});
            skLineSegment(sketch, "E103.4.14", {"start": v(-0.57, -5.72) * mm, "end": v(-0.5, -5.81) * mm});
            skLineSegment(sketch, "E103.4.15", {"start": v(-1.17, -4.26) * mm, "end": v(-1.16, -4.35) * mm});
            skLineSegment(sketch, "E103.4.16", {"start": v(-3.26, -3.22) * mm, "end": v(-3.35, -3.25) * mm});
            skLineSegment(sketch, "E103.4.17", {"start": v(-2.45, -2.33) * mm, "end": v(-2.53, -2.4) * mm});
            skLineSegment(sketch, "E103.4.18", {"start": v(-2.9, -2.85) * mm, "end": v(-2.97, -2.96) * mm});
            skLineSegment(sketch, "E103.4.19", {"start": v(-0.5, -5.81) * mm, "end": v(-0.43, -5.9) * mm});
            skLineSegment(sketch, "E103.4.20", {"start": v(-1.16, -4.35) * mm, "end": v(-1.15, -4.43) * mm});
            skLineSegment(sketch, "E103.4.21", {"start": v(-1.67, -2.13) * mm, "end": v(-1.76, -2.12) * mm});
            skLineSegment(sketch, "E103.4.22", {"start": v(-2.97, -2.96) * mm, "end": v(-3.03, -3.1) * mm});
            skLineSegment(sketch, "E103.4.23", {"start": v(-2.84, -2.74) * mm, "end": v(-2.9, -2.85) * mm});
            skLineSegment(sketch, "E103.4.24", {"start": v(-0.35, -5.99) * mm, "end": v(-0.28, -6) * mm});
            skLineSegment(sketch, "E103.4.25", {"start": v(-1.14, -4.52) * mm, "end": v(-1.12, -4.61) * mm});
            skLineSegment(sketch, "E103.4.26", {"start": v(-3.44, -3.28) * mm, "end": v(-3.53, -3.3) * mm});
            skLineSegment(sketch, "E103.4.27", {"start": v(-3.35, -3.25) * mm, "end": v(-3.44, -3.28) * mm});
            skLineSegment(sketch, "E103.4.28", {"start": v(-0.21, -6) * mm, "end": v(-0.14, -6) * mm});
            skLineSegment(sketch, "E103.4.29", {"start": v(-4.56, -3.37) * mm, "end": v(-4.67, -3.36) * mm});
            skLineSegment(sketch, "E103.4.30", {"start": v(-1.1, -4.7) * mm, "end": v(-1.07, -4.8) * mm});
            skLineSegment(sketch, "E103.4.31", {"start": v(-0.82, -2.9) * mm, "end": v(-0.8, -3) * mm});
            skLineSegment(sketch, "E103.4.32", {"start": v(-0.8, -3) * mm, "end": v(-0.8, -3.09) * mm});
            skLineSegment(sketch, "E103.4.33", {"start": v(-0.8, -3.09) * mm, "end": v(-0.8, -3.18) * mm});
            skLineSegment(sketch, "E103.4.34", {"start": v(-0.95, -3.82) * mm, "end": v(-1.01, -3.94) * mm});
            skLineSegment(sketch, "E103.4.35", {"start": v(-2.61, -2.46) * mm, "end": v(-2.69, -2.55) * mm});
            skLineSegment(sketch, "E103.4.36", {"start": v(-0.82, -5.35) * mm, "end": v(-0.76, -5.45) * mm});
            skLineSegment(sketch, "E103.4.37", {"start": v(-1.17, -2.37) * mm, "end": v(-1.07, -2.44) * mm});
            skLineSegment(sketch, "E103.4.38", {"start": v(-1.07, -2.44) * mm, "end": v(-1.01, -2.5) * mm});
            skLineSegment(sketch, "E103.4.39", {"start": v(-1.01, -2.5) * mm, "end": v(-0.96, -2.58) * mm});
            skLineSegment(sketch, "E103.4.40", {"start": v(-5.16, -3.06) * mm, "end": v(-5.2, -3) * mm});
            skLineSegment(sketch, "E103.4.41", {"start": v(-0.96, -2.58) * mm, "end": v(-0.91, -2.66) * mm});
            skLineSegment(sketch, "E103.4.42", {"start": v(-0.91, -2.66) * mm, "end": v(-0.88, -2.74) * mm});
            skLineSegment(sketch, "E103.4.43", {"start": v(-0.88, -2.74) * mm, "end": v(-0.84, -2.82) * mm});
            skLineSegment(sketch, "E103.4.44", {"start": v(-0.84, -2.82) * mm, "end": v(-0.82, -2.9) * mm});
            skLineSegment(sketch, "E103.4.45", {"start": v(-2.53, -2.4) * mm, "end": v(-2.61, -2.46) * mm});
            skLineSegment(sketch, "E103.4.46", {"start": v(-0.8, -3.18) * mm, "end": v(-0.8, -3.28) * mm});
            skLineSegment(sketch, "E103.4.47", {"start": v(-2.1, -2.16) * mm, "end": v(-2.2, -2.2) * mm});
            skLineSegment(sketch, "E103.4.48", {"start": v(-0.14, -6) * mm, "end": v(-0.07, -6) * mm});
            skLineSegment(sketch, "E103.4.49", {"start": v(-3.1, -3.14) * mm, "end": v(-3.18, -3.18) * mm});
            skLineSegment(sketch, "E103.4.50", {"start": v(-1.07, -4.8) * mm, "end": v(-1.04, -4.9) * mm});
            skLineSegment(sketch, "E103.4.51", {"start": v(-1.01, -3.94) * mm, "end": v(-1.08, -4.06) * mm});
            skLineSegment(sketch, "E103.4.52", {"start": v(-0.76, -5.45) * mm, "end": v(-0.7, -5.54) * mm});
            skLineSegment(sketch, "E103.4.53", {"start": v(-2.28, -2.23) * mm, "end": v(-2.36, -2.28) * mm});
            skLineSegment(sketch, "E103.4.54", {"start": v(-1.93, -2.13) * mm, "end": v(-2.02, -2.14) * mm});
            skLineSegment(sketch, "E103.4.55", {"start": v(-0.8, -3.28) * mm, "end": v(-0.8, -3.39) * mm});
            skLineSegment(sketch, "E103.4.56", {"start": v(-3.92, -3.37) * mm, "end": v(-4.02, -3.38) * mm});
            skLineSegment(sketch, "E103.4.57", {"start": v(-3.82, -3.36) * mm, "end": v(-3.92, -3.37) * mm});
            skLineSegment(sketch, "E103.4.58", {"start": v(-0.07, -6) * mm, "end": v(0, -6) * mm});
            skLineSegment(sketch, "E103.4.59", {"start": v(-1.04, -4.9) * mm, "end": v(-1, -4.98) * mm});
            skLineSegment(sketch, "E103.4.60", {"start": v(-3.53, -3.3) * mm, "end": v(-3.62, -3.32) * mm});
            skLineSegment(sketch, "E103.4.61", {"start": v(-3.18, -3.18) * mm, "end": v(-3.26, -3.22) * mm});
            skLineSegment(sketch, "E103.4.62", {"start": v(-4.12, -3.38) * mm, "end": v(-4.23, -3.38) * mm});
            skLineSegment(sketch, "E103.4.63", {"start": v(-3.62, -3.32) * mm, "end": v(-3.72, -3.34) * mm});
            skLineSegment(sketch, "E103.4.64", {"start": v(-0.8, -3.39) * mm, "end": v(-0.83, -3.5) * mm});
            skLineSegment(sketch, "E103.4.65", {"start": v(-1, -4.98) * mm, "end": v(-0.96, -5.08) * mm});
            skLineSegment(sketch, "E103.4.66", {"start": v(-4.78, -3.34) * mm, "end": v(-4.9, -3.32) * mm});
            skLineSegment(sketch, "E103.4.67", {"start": v(-0.83, -3.5) * mm, "end": v(-0.86, -3.6) * mm});
            skLineSegment(sketch, "E103.4.68", {"start": v(-5.12, -3.12) * mm, "end": v(-5.16, -3.06) * mm});
            skLineSegment(sketch, "E103.4.69", {"start": v(-4.02, -3.38) * mm, "end": v(-4.12, -3.38) * mm});
            skLineSegment(sketch, "E103.4.70", {"start": v(-0.96, -5.08) * mm, "end": v(-0.92, -5.17) * mm});
            skLineSegment(sketch, "E103.4.71", {"start": v(-5.09, -3.18) * mm, "end": v(-5.12, -3.12) * mm});
            skLineSegment(sketch, "E103.4.72", {"start": v(-0.86, -3.6) * mm, "end": v(-0.9, -3.71) * mm});
            skLineSegment(sketch, "E103.4.73", {"start": v(-4.34, -3.38) * mm, "end": v(-4.45, -3.38) * mm});
            skLineSegment(sketch, "E103.4.74", {"start": v(-3.72, -3.34) * mm, "end": v(-3.82, -3.36) * mm});
            skLineSegment(sketch, "E103.4.75", {"start": v(-0.92, -5.17) * mm, "end": v(-0.87, -5.26) * mm});
            skLineSegment(sketch, "E103.4.76", {"start": v(-2.36, -2.28) * mm, "end": v(-2.45, -2.33) * mm});
            skLineSegment(sketch, "E103.4.77", {"start": v(-4.45, -3.38) * mm, "end": v(-4.56, -3.37) * mm});
            skLineSegment(sketch, "E103.4.78", {"start": v(-1.17, -4.17) * mm, "end": v(-1.17, -4.26) * mm});
            skLineSegment(sketch, "E103.4.79", {"start": v(-1.76, -2.12) * mm, "end": v(-1.85, -2.12) * mm});
            skLineSegment(sketch, "E103.4.80", {"start": v(-0.9, -3.71) * mm, "end": v(-0.95, -3.82) * mm});
            skLineSegment(sketch, "E103.4.81", {"start": v(-2.2, -2.2) * mm, "end": v(-2.28, -2.23) * mm});
            skLineSegment(sketch, "E103.4.82", {"start": v(-2.02, -2.14) * mm, "end": v(-2.1, -2.16) * mm});
            skLineSegment(sketch, "E103.4.83", {"start": v(-0.87, -5.26) * mm, "end": v(-0.82, -5.35) * mm});
            skLineSegment(sketch, "E103.4.84", {"start": v(-5.01, -3.3) * mm, "end": v(-5.05, -3.24) * mm});
            skLineSegment(sketch, "E103.4.85", {"start": v(-2.76, -2.64) * mm, "end": v(-2.84, -2.74) * mm});
            skLineSegment(sketch, "E103.4.86", {"start": v(-2.69, -2.55) * mm, "end": v(-2.76, -2.64) * mm});
            skLineSegment(sketch, "E103.4.87", {"start": v(-1.47, -2.2) * mm, "end": v(-1.58, -2.15) * mm});
            skLineSegment(sketch, "E103.4.88", {"start": v(-1.36, -2.24) * mm, "end": v(-1.47, -2.2) * mm});
            skLineSegment(sketch, "E103.4.89", {"start": v(-1.34, -2.26) * mm, "end": v(-1.35, -2.25) * mm});
            skLineSegment(sketch, "E103.4.90", {"start": v(-1.31, -2.27) * mm, "end": v(-1.3, -2.28) * mm});
            skLineSegment(sketch, "E103.4.91", {"start": v(-1.27, -2.3) * mm, "end": v(-1.26, -2.3) * mm});
            skLineSegment(sketch, "E103.4.92", {"start": v(-1.26, -2.3) * mm, "end": v(-1.17, -2.37) * mm});
            skLineSegment(sketch, "E103.4.93", {"start": v(-1.28, -2.3) * mm, "end": v(-1.27, -2.3) * mm});
            skLineSegment(sketch, "E103.4.94", {"start": v(-1.3, -2.28) * mm, "end": v(-1.28, -2.3) * mm});
            skLineSegment(sketch, "E103.4.95", {"start": v(-1.3, -2.28) * mm, "end": v(-1.3, -2.28) * mm});
            skLineSegment(sketch, "E103.4.96", {"start": v(-1.31, -2.27) * mm, "end": v(-1.32, -2.27) * mm});
            skLineSegment(sketch, "E103.4.97", {"start": v(-1.32, -2.27) * mm, "end": v(-1.33, -2.26) * mm});
            skLineSegment(sketch, "E103.4.98", {"start": v(-1.33, -2.26) * mm, "end": v(-1.34, -2.26) * mm});
            skLineSegment(sketch, "E103.4.99", {"start": v(-1.35, -2.25) * mm, "end": v(-1.36, -2.24) * mm});
            skLineSegment(sketch, "E103.5.0", {"start": v(1.17, -4.17) * mm, "end": v(1.17, -4.26) * mm});
            skLineSegment(sketch, "E103.5.1", {"start": v(3.44, -3.28) * mm, "end": v(3.53, -3.3) * mm});
            skLineSegment(sketch, "E103.5.2", {"start": v(0.43, -5.9) * mm, "end": v(0.35, -5.99) * mm});
            skLineSegment(sketch, "E103.5.3", {"start": v(0.91, -2.66) * mm, "end": v(0.88, -2.74) * mm});
            skLineSegment(sketch, "E103.5.4", {"start": v(0.28, -6) * mm, "end": v(0.21, -6) * mm});
            skLineSegment(sketch, "E103.5.5", {"start": v(3.26, -3.22) * mm, "end": v(3.35, -3.25) * mm});
            skLineSegment(sketch, "E103.5.6", {"start": v(5.05, -3.24) * mm, "end": v(5.09, -3.18) * mm});
            skLineSegment(sketch, "E103.5.7", {"start": v(4.45, -3.38) * mm, "end": v(4.56, -3.37) * mm});
            skLineSegment(sketch, "E103.5.8", {"start": v(2.97, -2.96) * mm, "end": v(3.03, -3.1) * mm});
            skLineSegment(sketch, "E103.5.9", {"start": v(0.82, -5.35) * mm, "end": v(0.76, -5.45) * mm});
            skLineSegment(sketch, "E103.5.10", {"start": v(1.07, -2.44) * mm, "end": v(1.01, -2.5) * mm});
            skLineSegment(sketch, "E103.5.11", {"start": v(4.9, -3.32) * mm, "end": v(5.01, -3.3) * mm});
            skLineSegment(sketch, "E103.5.12", {"start": v(4.56, -3.37) * mm, "end": v(4.67, -3.36) * mm});
            skLineSegment(sketch, "E103.5.13", {"start": v(0.57, -5.72) * mm, "end": v(0.5, -5.81) * mm});
            skLineSegment(sketch, "E103.5.14", {"start": v(4.67, -3.36) * mm, "end": v(4.78, -3.34) * mm});
            skLineSegment(sketch, "E103.5.15", {"start": v(3.1, -3.14) * mm, "end": v(3.18, -3.18) * mm});
            skLineSegment(sketch, "E103.5.16", {"start": v(1.15, -4.43) * mm, "end": v(1.14, -4.52) * mm});
            skLineSegment(sketch, "E103.5.17", {"start": v(0.8, -3.28) * mm, "end": v(0.8, -3.39) * mm});
            skLineSegment(sketch, "E103.5.18", {"start": v(1.01, -3.94) * mm, "end": v(1.08, -4.06) * mm});
            skLineSegment(sketch, "E103.5.19", {"start": v(4.78, -3.34) * mm, "end": v(4.9, -3.32) * mm});
            skLineSegment(sketch, "E103.5.20", {"start": v(3.18, -3.18) * mm, "end": v(3.26, -3.22) * mm});
            skLineSegment(sketch, "E103.5.21", {"start": v(1.01, -2.5) * mm, "end": v(0.96, -2.58) * mm});
            skLineSegment(sketch, "E103.5.22", {"start": v(1.08, -4.06) * mm, "end": v(1.17, -4.17) * mm});
            skLineSegment(sketch, "E103.5.23", {"start": v(0.95, -3.82) * mm, "end": v(1.01, -3.94) * mm});
            skLineSegment(sketch, "E103.5.24", {"start": v(5.01, -3.3) * mm, "end": v(5.05, -3.24) * mm});
            skLineSegment(sketch, "E103.5.25", {"start": v(3.35, -3.25) * mm, "end": v(3.44, -3.28) * mm});
            skLineSegment(sketch, "E103.5.26", {"start": v(1.12, -4.61) * mm, "end": v(1.1, -4.7) * mm});
            skLineSegment(sketch, "E103.5.27", {"start": v(1.14, -4.52) * mm, "end": v(1.12, -4.61) * mm});
            skLineSegment(sketch, "E103.5.28", {"start": v(5.09, -3.18) * mm, "end": v(5.12, -3.12) * mm});
            skLineSegment(sketch, "E103.5.29", {"start": v(0.64, -5.63) * mm, "end": v(0.57, -5.72) * mm});
            skLineSegment(sketch, "E103.5.30", {"start": v(3.53, -3.3) * mm, "end": v(3.62, -3.32) * mm});
            skLineSegment(sketch, "E103.5.31", {"start": v(2.1, -2.16) * mm, "end": v(2.2, -2.2) * mm});
            skLineSegment(sketch, "E103.5.32", {"start": v(2.2, -2.2) * mm, "end": v(2.28, -2.23) * mm});
            skLineSegment(sketch, "E103.5.33", {"start": v(2.28, -2.23) * mm, "end": v(2.36, -2.28) * mm});
            skLineSegment(sketch, "E103.5.34", {"start": v(2.84, -2.74) * mm, "end": v(2.9, -2.85) * mm});
            skLineSegment(sketch, "E103.5.35", {"start": v(0.83, -3.5) * mm, "end": v(0.86, -3.6) * mm});
            skLineSegment(sketch, "E103.5.36", {"start": v(4.23, -3.38) * mm, "end": v(4.34, -3.38) * mm});
            skLineSegment(sketch, "E103.5.37", {"start": v(1.47, -2.2) * mm, "end": v(1.58, -2.15) * mm});
            skLineSegment(sketch, "E103.5.38", {"start": v(1.58, -2.15) * mm, "end": v(1.67, -2.13) * mm});
            skLineSegment(sketch, "E103.5.39", {"start": v(1.67, -2.13) * mm, "end": v(1.76, -2.12) * mm});
            skLineSegment(sketch, "E103.5.40", {"start": v(0.07, -6) * mm, "end": v(0, -6) * mm});
            skLineSegment(sketch, "E103.5.41", {"start": v(1.76, -2.12) * mm, "end": v(1.85, -2.12) * mm});
            skLineSegment(sketch, "E103.5.42", {"start": v(1.85, -2.12) * mm, "end": v(1.93, -2.13) * mm});
            skLineSegment(sketch, "E103.5.43", {"start": v(1.93, -2.13) * mm, "end": v(2.02, -2.14) * mm});
            skLineSegment(sketch, "E103.5.44", {"start": v(2.02, -2.14) * mm, "end": v(2.1, -2.16) * mm});
            skLineSegment(sketch, "E103.5.45", {"start": v(0.8, -3.39) * mm, "end": v(0.83, -3.5) * mm});
            skLineSegment(sketch, "E103.5.46", {"start": v(2.36, -2.28) * mm, "end": v(2.45, -2.33) * mm});
            skLineSegment(sketch, "E103.5.47", {"start": v(0.82, -2.9) * mm, "end": v(0.8, -3) * mm});
            skLineSegment(sketch, "E103.5.48", {"start": v(5.12, -3.12) * mm, "end": v(5.16, -3.06) * mm});
            skLineSegment(sketch, "E103.5.49", {"start": v(1.17, -4.26) * mm, "end": v(1.16, -4.35) * mm});
            skLineSegment(sketch, "E103.5.50", {"start": v(3.62, -3.32) * mm, "end": v(3.72, -3.34) * mm});
            skLineSegment(sketch, "E103.5.51", {"start": v(2.9, -2.85) * mm, "end": v(2.97, -2.96) * mm});
            skLineSegment(sketch, "E103.5.52", {"start": v(4.34, -3.38) * mm, "end": v(4.45, -3.38) * mm});
            skLineSegment(sketch, "E103.5.53", {"start": v(0.8, -3.09) * mm, "end": v(0.8, -3.18) * mm});
            skLineSegment(sketch, "E103.5.54", {"start": v(0.88, -2.74) * mm, "end": v(0.84, -2.82) * mm});
            skLineSegment(sketch, "E103.5.55", {"start": v(2.45, -2.33) * mm, "end": v(2.53, -2.4) * mm});
            skLineSegment(sketch, "E103.5.56", {"start": v(0.96, -5.08) * mm, "end": v(0.92, -5.17) * mm});
            skLineSegment(sketch, "E103.5.57", {"start": v(1, -4.98) * mm, "end": v(0.96, -5.08) * mm});
            skLineSegment(sketch, "E103.5.58", {"start": v(5.16, -3.06) * mm, "end": v(5.2, -3) * mm});
            skLineSegment(sketch, "E103.5.59", {"start": v(3.72, -3.34) * mm, "end": v(3.82, -3.36) * mm});
            skLineSegment(sketch, "E103.5.60", {"start": v(1.1, -4.7) * mm, "end": v(1.07, -4.8) * mm});
            skLineSegment(sketch, "E103.5.61", {"start": v(1.16, -4.35) * mm, "end": v(1.15, -4.43) * mm});
            skLineSegment(sketch, "E103.5.62", {"start": v(0.87, -5.26) * mm, "end": v(0.82, -5.35) * mm});
            skLineSegment(sketch, "E103.5.63", {"start": v(1.07, -4.8) * mm, "end": v(1.04, -4.9) * mm});
            skLineSegment(sketch, "E103.5.64", {"start": v(2.53, -2.4) * mm, "end": v(2.61, -2.46) * mm});
            skLineSegment(sketch, "E103.5.65", {"start": v(3.82, -3.36) * mm, "end": v(3.92, -3.37) * mm});
            skLineSegment(sketch, "E103.5.66", {"start": v(0.5, -5.81) * mm, "end": v(0.43, -5.9) * mm});
            skLineSegment(sketch, "E103.5.67", {"start": v(2.61, -2.46) * mm, "end": v(2.69, -2.55) * mm});
            skLineSegment(sketch, "E103.5.68", {"start": v(0.14, -6) * mm, "end": v(0.07, -6) * mm});
            skLineSegment(sketch, "E103.5.69", {"start": v(0.92, -5.17) * mm, "end": v(0.87, -5.26) * mm});
            skLineSegment(sketch, "E103.5.70", {"start": v(3.92, -3.37) * mm, "end": v(4.02, -3.38) * mm});
            skLineSegment(sketch, "E103.5.71", {"start": v(0.21, -6) * mm, "end": v(0.14, -6) * mm});
            skLineSegment(sketch, "E103.5.72", {"start": v(2.69, -2.55) * mm, "end": v(2.76, -2.64) * mm});
            skLineSegment(sketch, "E103.5.73", {"start": v(0.76, -5.45) * mm, "end": v(0.7, -5.54) * mm});
            skLineSegment(sketch, "E103.5.74", {"start": v(1.04, -4.9) * mm, "end": v(1, -4.98) * mm});
            skLineSegment(sketch, "E103.5.75", {"start": v(4.02, -3.38) * mm, "end": v(4.12, -3.38) * mm});
            skLineSegment(sketch, "E103.5.76", {"start": v(0.8, -3.18) * mm, "end": v(0.8, -3.28) * mm});
            skLineSegment(sketch, "E103.5.77", {"start": v(0.7, -5.54) * mm, "end": v(0.64, -5.63) * mm});
            skLineSegment(sketch, "E103.5.78", {"start": v(3.03, -3.1) * mm, "end": v(3.1, -3.14) * mm});
            skLineSegment(sketch, "E103.5.79", {"start": v(0.96, -2.58) * mm, "end": v(0.91, -2.66) * mm});
            skLineSegment(sketch, "E103.5.80", {"start": v(2.76, -2.64) * mm, "end": v(2.84, -2.74) * mm});
            skLineSegment(sketch, "E103.5.81", {"start": v(0.8, -3) * mm, "end": v(0.8, -3.09) * mm});
            skLineSegment(sketch, "E103.5.82", {"start": v(0.84, -2.82) * mm, "end": v(0.82, -2.9) * mm});
            skLineSegment(sketch, "E103.5.83", {"start": v(4.12, -3.38) * mm, "end": v(4.23, -3.38) * mm});
            skLineSegment(sketch, "E103.5.84", {"start": v(0.35, -5.99) * mm, "end": v(0.28, -6) * mm});
            skLineSegment(sketch, "E103.5.85", {"start": v(0.9, -3.71) * mm, "end": v(0.95, -3.82) * mm});
            skLineSegment(sketch, "E103.5.86", {"start": v(0.86, -3.6) * mm, "end": v(0.9, -3.71) * mm});
            skLineSegment(sketch, "E103.5.87", {"start": v(1.17, -2.37) * mm, "end": v(1.07, -2.44) * mm});
            skLineSegment(sketch, "E103.5.88", {"start": v(1.26, -2.3) * mm, "end": v(1.17, -2.37) * mm});
            skLineSegment(sketch, "E103.5.89", {"start": v(1.28, -2.3) * mm, "end": v(1.27, -2.3) * mm});
            skLineSegment(sketch, "E103.5.90", {"start": v(1.31, -2.27) * mm, "end": v(1.32, -2.27) * mm});
            skLineSegment(sketch, "E103.5.91", {"start": v(1.35, -2.25) * mm, "end": v(1.36, -2.24) * mm});
            skLineSegment(sketch, "E103.5.92", {"start": v(1.36, -2.24) * mm, "end": v(1.47, -2.2) * mm});
            skLineSegment(sketch, "E103.5.93", {"start": v(1.34, -2.26) * mm, "end": v(1.35, -2.25) * mm});
            skLineSegment(sketch, "E103.5.94", {"start": v(1.33, -2.26) * mm, "end": v(1.34, -2.26) * mm});
            skLineSegment(sketch, "E103.5.95", {"start": v(1.32, -2.27) * mm, "end": v(1.33, -2.26) * mm});
            skLineSegment(sketch, "E103.5.96", {"start": v(1.31, -2.27) * mm, "end": v(1.3, -2.28) * mm});
            skLineSegment(sketch, "E103.5.97", {"start": v(1.3, -2.28) * mm, "end": v(1.3, -2.28) * mm});
            skLineSegment(sketch, "E103.5.98", {"start": v(1.3, -2.28) * mm, "end": v(1.28, -2.3) * mm});
            skLineSegment(sketch, "E103.5.99", {"start": v(1.27, -2.3) * mm, "end": v(1.26, -2.3) * mm});
            skCircle(sketch, "E104", {"center": v(0, 0) * mm, "radius": 4.5 * mm, "construction": true});
            skCircle(sketch, "E105", {"center": v(0, 0) * mm, "radius": 1.5 * mm});
            skSolve(sketch);
        }
        {
            var Q0;
            Q0=makeQuery(id+"F0.imprint","IMPRINT",FACE,{"disambiguationData":[TD([[makeQuery(id+"F0.imprint","IMPRINT",EDGE,{"derivedFrom":sQuery(id+"F0.wireOp",EDGE,"E0")}),1.0]])]});
            extrude(context, id + "F1", {"entities" : qUnion([Q0]), "depth" : 3 * mm});
        }
    });
